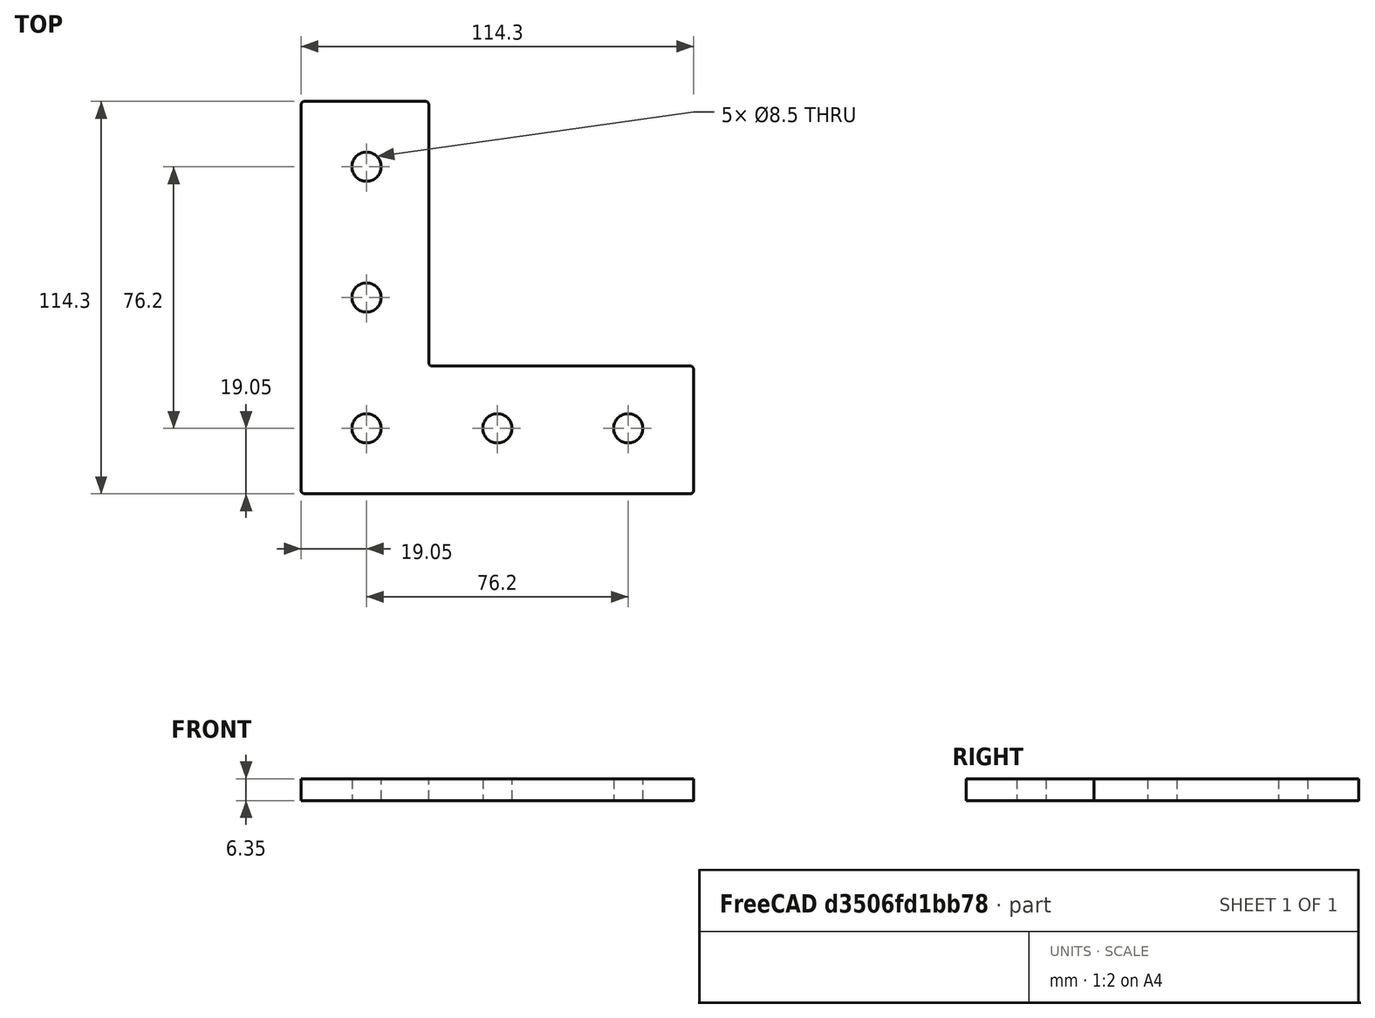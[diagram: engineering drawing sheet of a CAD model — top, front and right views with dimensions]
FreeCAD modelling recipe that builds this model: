
FCSTD DOCUMENT  (FreeCAD 0.18R)
Label: 1515-corner-plate-5
License: All rights reserved
LicenseURL: http://en.wikipedia.org/wiki/All_rights_reserved
objects: Sketcher::SketchObject×1, PartDesign::Pad×1, PartDesign::Body×1
note: 4 computed .brp shape members not serialized (recipe doc carries the construction recipe); baked Part::Feature solids carry a one-line shape summary decoded from their .brp

FEATURE [Sketcher::SketchObject] Sketch
  MapMode = 5
  Support = -> [XY_Plane]
  sketch-geometry (17):
    g0: LineSegment StartX=-113.3 StartY=114.3 StartZ=0 EndX=-78.1144 EndY=114.3 EndZ=0
    g1: LineSegment StartX=-77.1144 StartY=113.3 StartZ=0 EndX=-77.1144 EndY=38.1856 EndZ=0
    g2: LineSegment StartX=-76.1144 StartY=37.1856 StartZ=0 EndX=-1 EndY=37.1856 EndZ=0
    g3: LineSegment StartX=-8.7e-15 StartY=36.1856 StartZ=0 EndX=0 EndY=1 EndZ=0
    g4: LineSegment StartX=-1 StartY=0 StartZ=0 EndX=-113.3 EndY=0 EndZ=0
    g5: LineSegment StartX=-114.3 StartY=113.3 StartZ=0 EndX=-114.3 EndY=1 EndZ=0
    g6: ArcOfCircle CenterX=-113.3 CenterY=113.3 CenterZ=0 NormalX=0 NormalY=0 NormalZ=1 AngleXU=0 Radius=1 StartAngle=1.5708 EndAngle=3.14159
    g7: ArcOfCircle CenterX=-78.1144 CenterY=113.3 CenterZ=0 NormalX=0 NormalY=0 NormalZ=1 AngleXU=0 Radius=1 StartAngle=4.4e-15 EndAngle=1.5708
    g8: ArcOfCircle CenterX=-76.1144 CenterY=38.1856 CenterZ=0 NormalX=0 NormalY=0 NormalZ=1 AngleXU=0 Radius=1 StartAngle=3.14159 EndAngle=4.71239
    g9: ArcOfCircle CenterX=-1 CenterY=36.1856 CenterZ=0 NormalX=0 NormalY=0 NormalZ=1 AngleXU=0 Radius=1 StartAngle=-2.7e-15 EndAngle=1.5708
    g10: ArcOfCircle CenterX=-1 CenterY=1 CenterZ=0 NormalX=0 NormalY=0 NormalZ=1 AngleXU=0 Radius=1 StartAngle=4.71239 EndAngle=6.28319
    g11: ArcOfCircle CenterX=-113.3 CenterY=1 CenterZ=0 NormalX=0 NormalY=0 NormalZ=1 AngleXU=0 Radius=1 StartAngle=3.14159 EndAngle=4.71239
    g12: Circle CenterX=-19.05 CenterY=19.05 CenterZ=0 NormalX=0 NormalY=0 NormalZ=1 AngleXU=0 Radius=4.25
    g13: Circle CenterX=-57.15 CenterY=19.05 CenterZ=0 NormalX=0 NormalY=0 NormalZ=1 AngleXU=0 Radius=4.25
    g14: Circle CenterX=-95.25 CenterY=19.05 CenterZ=0 NormalX=0 NormalY=0 NormalZ=1 AngleXU=0 Radius=4.25
    g15: Circle CenterX=-95.25 CenterY=57.15 CenterZ=0 NormalX=0 NormalY=0 NormalZ=1 AngleXU=0 Radius=4.25
    g16: Circle CenterX=-95.25 CenterY=95.25 CenterZ=0 NormalX=0 NormalY=0 NormalZ=1 AngleXU=0 Radius=4.25
  constraints (45):
    c: Horizontal(g0)
    c: Vertical(g1)
    c: Horizontal(g2)
    c: Vertical(g5)
    c: Tangent(g5,g6) = -1.5708
    c: Tangent(g0,g6) = 1.5708
    c: Tangent(g0,g7) = 1.5708
    c: Tangent(g1,g7) = 1.5708
    c: DistanceY(g-1,g0) = 114.3
    c: DistanceX(g1,g-1) = 77.1144
    c: DistanceY(g1,g0) = 1
    c: DistanceY(g5,g1) = 0
    c: Tangent(g1,g8) = -1.5708
    c: Tangent(g2,g8) = -1.5708
    c: Tangent(g2,g9) = 1.5708
    c: Tangent(g3,g9) = 1.5708
    c: Tangent(g3,g10) = 1.5708
    c: Tangent(g4,g10) = 1.5708
    c: Tangent(g5,g11) = -1.5708
    c: Tangent(g4,g11) = 1.5708
    c: DistanceY(g4,g5) = 1
    c: Horizontal(g4)
    c: DistanceX(g3,g-1) = 0
    c: DistanceY(g4,g-1) = 0
    c: DistanceY(g3,g2) = 1
    c: DistanceY(g2,g1) = 1
    c: DistanceY(g4,g3) = 1
    c: DistanceX(g4,g-1) = 1
    c: DistanceY(g-1,g2) = 37.1856
    c: Diameter(g12) = 8.5
    c: DistanceY(g-1,g12) = 19.05
    c: DistanceX(g12,g-1) = 19.05
    c: Equal(g13,g12)
    c: DistanceX(g13,g12) = 38.1
    c: DistanceY(g12,g13) = 0
    c: Equal(g14,g12)
    c: Equal(g15,g12)
    c: Equal(g16,g12)
    c: DistanceX(g15,g14) = 0
    c: DistanceX(g16,g14) = 0
    c: DistanceY(g15,g16) = 38.1
    c: DistanceY(g14,g15) = 38.1
    c: DistanceY(g13,g14) = 0
    c: DistanceX(g5,g1) = 37.1856
    c: DistanceX(g14,g13) = 38.1
FEATURE [PartDesign::Pad] Pad
  Length = 6.35
  Length2 = 100
  Profile = -> Sketch
  Type = 0
FEATURE [PartDesign::Body] Body  label="1515-corner-plate-5"
  Group = -> [Sketch,Pad]
  Origin = -> Origin
  Tip = -> Pad
